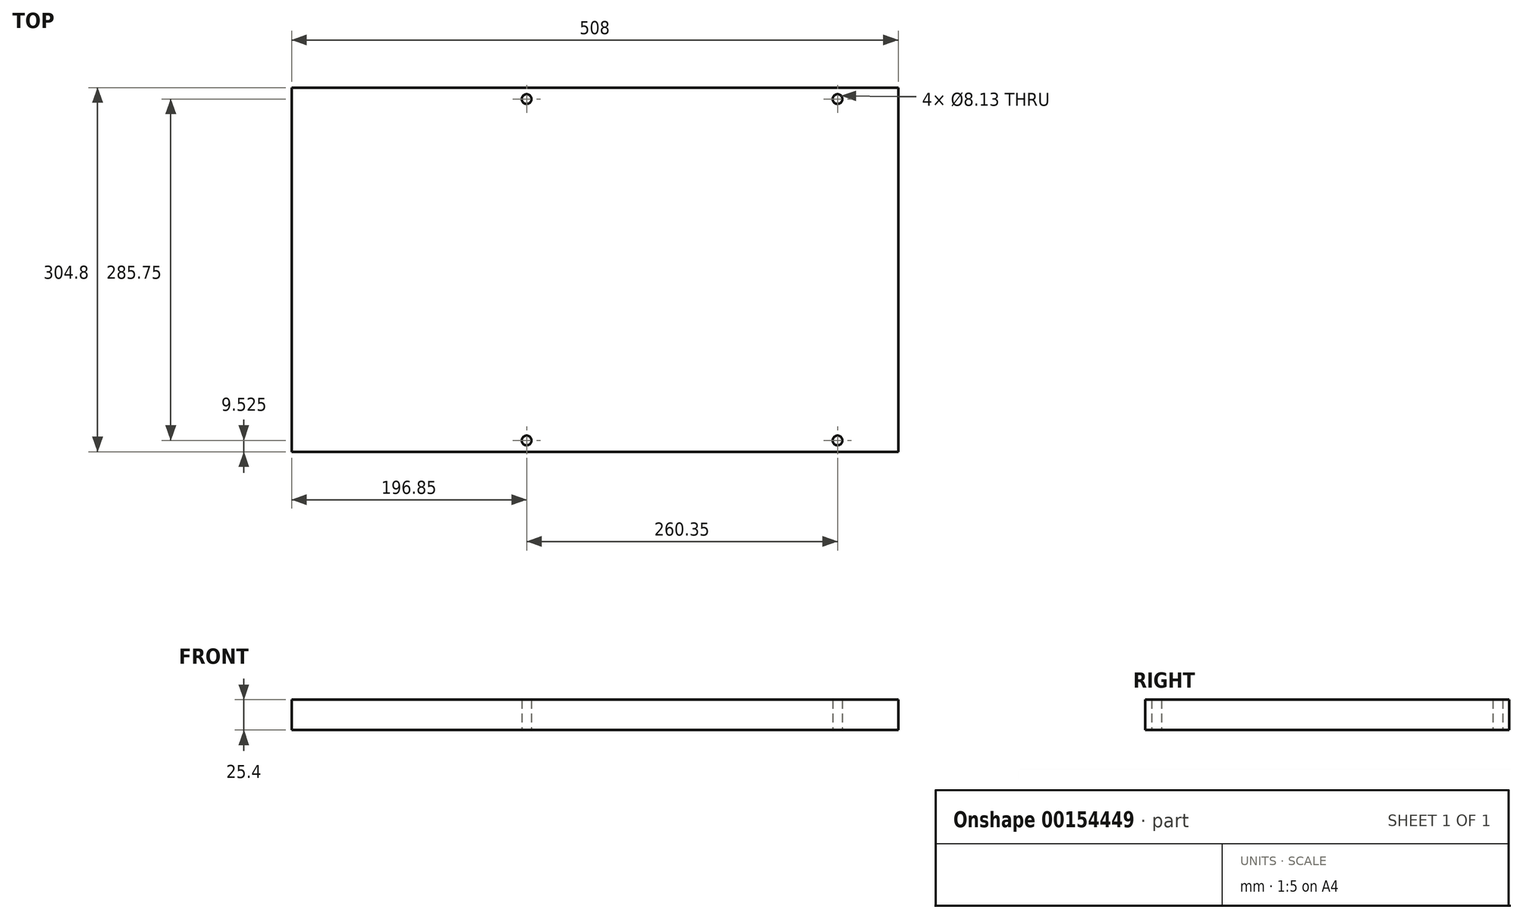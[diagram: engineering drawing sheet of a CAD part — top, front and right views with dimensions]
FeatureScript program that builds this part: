
annotation { "Feature Type Name" : "Feature", "Feature Type Description" : "" }
export const myFeature = defineFeature(function(context is Context, id is Id, definition is map)
    precondition{}
    {
        {
            var Q0;
            Q0=qCreatedBy(makeId("Top.planeOp"),FACE);
            var sketch = newSketch(context, id + "F0", { "sketchPlane" : qUnion([Q0])});
            skLineSegment(sketch, "E0.bottom", {"start": v(-254, 152.4) * mm, "end": v(254, 152.4) * mm});
            skLineSegment(sketch, "E0.top", {"start": v(-254, -152.4) * mm, "end": v(254, -152.4) * mm});
            skLineSegment(sketch, "E0.left", {"start": v(-254, 152.4) * mm, "end": v(-254, -152.4) * mm});
            skLineSegment(sketch, "E0.right", {"start": v(254, 152.4) * mm, "end": v(254, -152.4) * mm});
            skLineSegment(sketch, "E1", {"start": v(-254, 152.4) * mm, "end": v(254, -152.4) * mm, "construction": true});
            skSolve(sketch);
        }
        {
            var Q0;
            Q0=makeQuery(id+"F0.imprint","IMPRINT",FACE,{"disambiguationData":[TD([[makeQuery(id+"F0.imprint","IMPRINT",EDGE,{"derivedFrom":sQuery(id+"F0.wireOp",EDGE,"E0.bottom")}),-1.0]])]});
            extrude(context, id + "F1", {"entities" : qUnion([Q0]), "depth" : 25.4 * mm});
        }
        {
            var Q0;
            Q0=makeQuery(id+"F1.opExtrude","CAP_FACE",FACE,{"disambiguationData":[OSD([sQuery(id+"F0.wireOp",EDGE,"E0.bottom"),sQuery(id+"F0.wireOp",EDGE,"E0.top"),sQuery(id+"F0.wireOp",EDGE,"E0.left"),sQuery(id+"F0.wireOp",EDGE,"E0.right")])],"isStart":true});
            var sketch = newSketch(context, id + "F2", { "sketchPlane" : qUnion([Q0])});
            skLineSegment(sketch, "E2", {"start": v(203.2, 152.4) * mm, "end": v(203.2, -152.4) * mm, "construction": true});
            skLineSegment(sketch, "E3", {"start": v(-57.15, 152.4) * mm, "end": v(-57.15, -152.4) * mm, "construction": true});
            skLineSegment(sketch, "E4", {"start": v(-275.83, 0) * mm, "end": v(283.64, 0) * mm, "construction": true});
            skPoint(sketch, "E4.startSnap0", {"position": v(-254, 0) * mm});
            skPoint(sketch, "E4.endSnap0", {"position": v(254, 0) * mm});
            skLineSegment(sketch, "E5", {"start": v(-254, 142.87) * mm, "end": v(254, 142.87) * mm, "construction": true});
            skLineSegment(sketch, "E6", {"start": v(-254, -142.88) * mm, "end": v(254, -142.88) * mm, "construction": true});
            skCircle(sketch, "E7", {"center": v(-57.15, 142.87) * mm, "radius": 4.06 * mm});
            skCircle(sketch, "E8", {"center": v(203.2, 142.87) * mm, "radius": 4.06 * mm});
            skCircle(sketch, "E9", {"center": v(203.2, -142.88) * mm, "radius": 4.06 * mm});
            skCircle(sketch, "E10", {"center": v(-57.15, -142.88) * mm, "radius": 4.06 * mm});
            skSolve(sketch);
        }
        {
            var Q0;
            Q0=makeQuery(id+"F2.imprint","IMPRINT",FACE,{"disambiguationData":[TD([[makeQuery(id+"F2.imprint","IMPRINT",EDGE,{"derivedFrom":sQuery(id+"F2.wireOp",EDGE,"E7")}),1.0]])]});
            var Q1;
            Q1=makeQuery(id+"F2.imprint","IMPRINT",FACE,{"disambiguationData":[TD([[makeQuery(id+"F2.imprint","IMPRINT",EDGE,{"derivedFrom":sQuery(id+"F2.wireOp",EDGE,"E8")}),1.0]])]});
            var Q2;
            Q2=makeQuery(id+"F2.imprint","IMPRINT",FACE,{"disambiguationData":[TD([[makeQuery(id+"F2.imprint","IMPRINT",EDGE,{"derivedFrom":sQuery(id+"F2.wireOp",EDGE,"E9")}),1.0]])]});
            var Q3;
            Q3=makeQuery(id+"F2.imprint","IMPRINT",FACE,{"disambiguationData":[TD([[makeQuery(id+"F2.imprint","IMPRINT",EDGE,{"derivedFrom":sQuery(id+"F2.wireOp",EDGE,"E10")}),1.0]])]});
            extrude(context, id + "F3", {"entities" : qUnion([Q0, Q1, Q2, Q3]), "operationType" : NewBodyOperationType.REMOVE, "endBound" : BoundingType.THROUGH_ALL, "oppositeDirection" : true, "depth" : 25.4 * mm});
        }
    });
